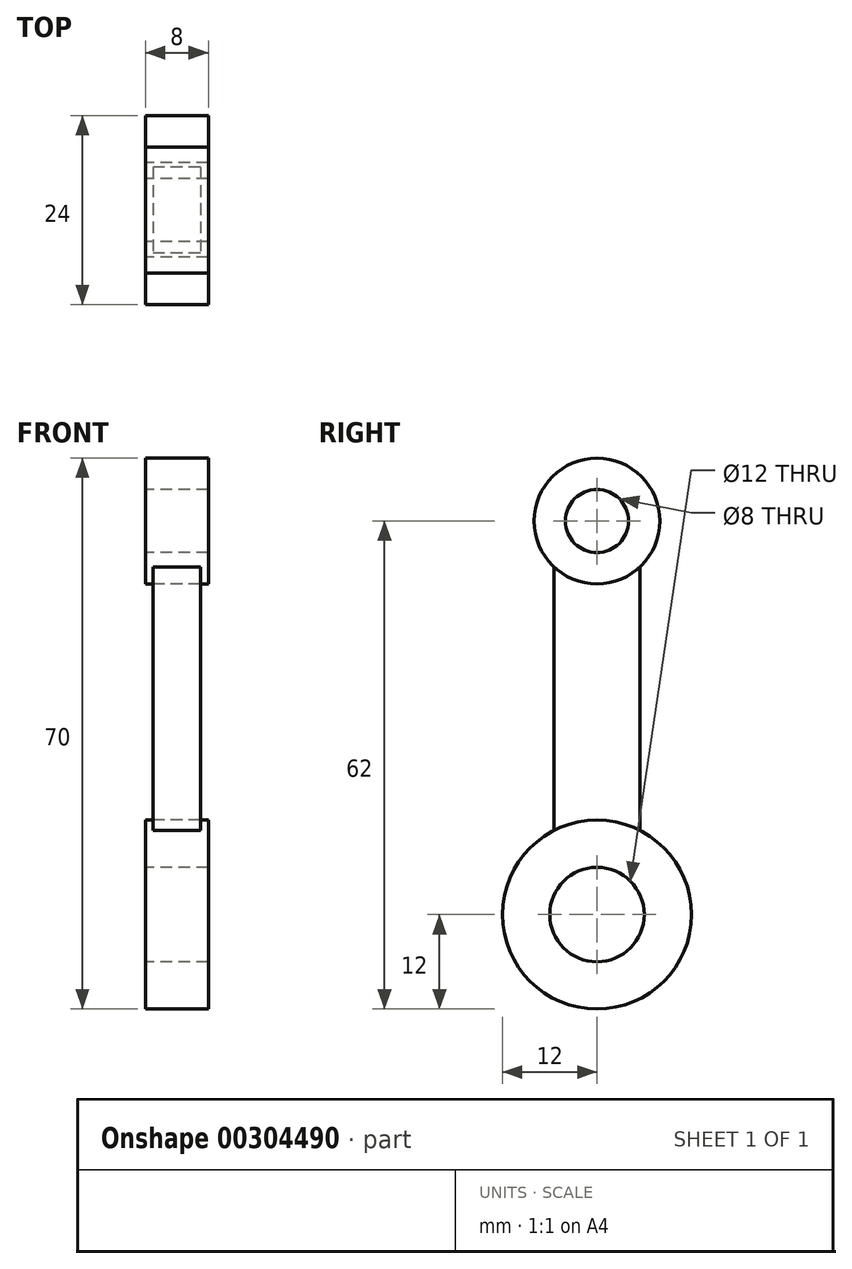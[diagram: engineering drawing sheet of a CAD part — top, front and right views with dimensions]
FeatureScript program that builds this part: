
annotation { "Feature Type Name" : "Feature", "Feature Type Description" : "" }
export const myFeature = defineFeature(function(context is Context, id is Id, definition is map)
    precondition{}
    {
        {
            var Q0;
            Q0=qCreatedBy(makeId("Right.planeOp"),FACE);
            var sketch = newSketch(context, id + "F0", { "sketchPlane" : qUnion([Q0])});
            skCircle(sketch, "E0", {"center": v(0, 0) * mm, "radius": 6 * mm});
            skCircle(sketch, "E1", {"center": v(0, 0) * mm, "radius": 12 * mm});
            skLineSegment(sketch, "E2", {"start": v(0, 0) * mm, "end": v(0, 50) * mm, "construction": true});
            skCircle(sketch, "E3", {"center": v(0, 50) * mm, "radius": 4 * mm});
            skCircle(sketch, "E4", {"center": v(0, 50) * mm, "radius": 8 * mm});
            skLineSegment(sketch, "E5", {"start": v(-5.46, 44.15) * mm, "end": v(-5.46, 10.69) * mm});
            skLineSegment(sketch, "E6.MirrorCS", {"start": v(5.46, 44.15) * mm, "end": v(5.46, 10.69) * mm});
            skSolve(sketch);
        }
        {
            var Q0;
            Q0=makeQuery(id+"F0.imprint","IMPRINT",FACE,{"disambiguationData":[TD([[makeQuery(id+"F0.imprint","IMPRINT",EDGE,{"derivedFrom":sQuery(id+"F0.wireOp",EDGE,"E0")}),-1.0]])]});
            var Q1;
            Q1=makeQuery(id+"F0.imprint","IMPRINT",FACE,{"disambiguationData":[TD([[makeQuery(id+"F0.imprint","IMPRINT",EDGE,{"derivedFrom":sQuery(id+"F0.wireOp",EDGE,"E3")}),-1.0]])]});
            extrude(context, id + "F1", {"entities" : qUnion([Q0, Q1]), "depth" : 8 * mm, "symmetric" : true});
        }
        {
            var Q0;
            {var subQ0=sQuery(id+"F0.wireOp",EDGE,"E5");Q0=makeQuery(id+"F0.imprint","IMPRINT",FACE,{"disambiguationData":[TD([[makeQuery(id+"F0.imprint","IMPRINT",EDGE,{"derivedFrom":subQ0}),1.0]])]});}
            extrude(context, id + "F2", {"entities" : qUnion([Q0]), "depth" : 6 * mm, "symmetric" : true});
        }
    });
